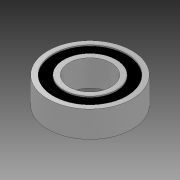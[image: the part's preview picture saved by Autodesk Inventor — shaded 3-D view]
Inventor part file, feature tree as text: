
AUTODESK INVENTOR PART (.ipt)
format: ipt  version: 2020 (Build 240168000, 168)  size: 131,072 bytes
history: native  units: mm
features: revolve x1, sketch x1
ambient origin geometry x8: Origin, YZ Plane, XZ Plane, XY Plane, X Axis, Y Axis, Z Axis, Center Point
bodies: Solid1 (feature_tree)
feature tree (2):
  revolve  "Revolution1"  [1 undecoded]
  sketch  "Sketch1"  dims[d0=4.0mm d2=5.0mm d5=8.0mm d6=0.2mm d7=1.0mm d8=90.0deg]
note: 1 required parameter value undecoded (feature->parameter linkage not recoverable at this tier; creation-order binding heuristic only, values carry confidence <= 0.55)
